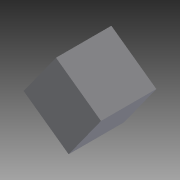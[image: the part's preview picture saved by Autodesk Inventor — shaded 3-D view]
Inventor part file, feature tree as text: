
AUTODESK INVENTOR PART (.ipt)
format: ipt  version: 2015 (Build 190159000, 159)  size: 87,552 bytes
history: native  units: in
note: dims shown in document units (in); Inventor stores cm internally (conversion verified against a paired STEP export)
features: extrude x1, sketch x1
ambient origin geometry x8: Origin, YZ Plane, XZ Plane, XY Plane, X Axis, Y Axis, Z Axis, Center Point
bodies: Body1 (feature_tree)
feature tree (2):
  extrude  "Extrusion3"  [1 undecoded]
  sketch  "Sketch3"  dims[d7=0.0in]
note: 1 required parameter value undecoded (feature->parameter linkage not recoverable at this tier; creation-order binding heuristic only, values carry confidence <= 0.55)
